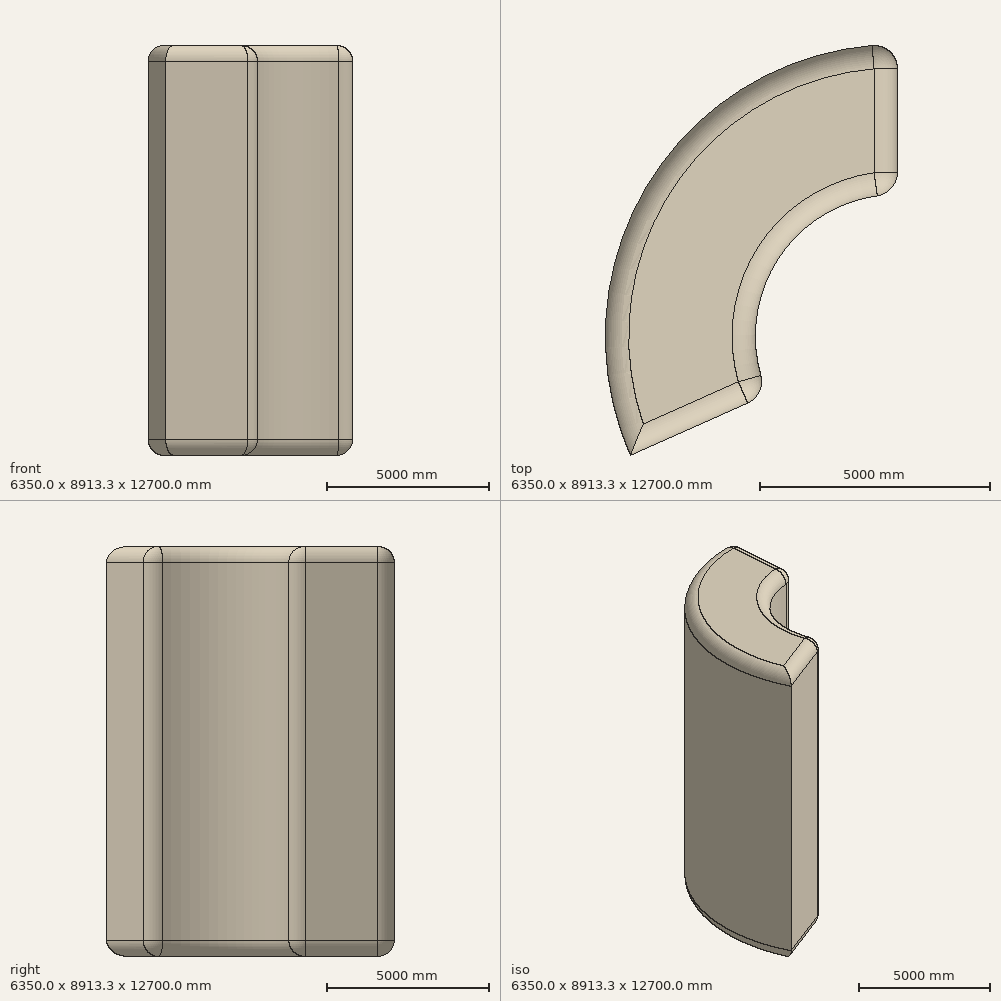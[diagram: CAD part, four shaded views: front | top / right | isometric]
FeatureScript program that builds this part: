
annotation { "Feature Type Name" : "Feature", "Feature Type Description" : "" }
export const myFeature = defineFeature(function(context is Context, id is Id, definition is map)
    precondition{}
    {
        {
            var Q0;
            Q0=qCreatedBy(makeId("Top.planeOp"),FACE);
            var sketch = newSketch(context, id + "F0", { "sketchPlane" : qUnion([Q0])});
            skArc(sketch, "E0", {"start": v(0, 6350) * mm, "mid": v(-5326.35, 3457.24) * mm, "end": v(-5799.83, -2585.43) * mm});
            skLineSegment(sketch, "E1", {"start": v(0, 3087.9) * mm, "end": v(0, 6350) * mm});
            skLineSegment(sketch, "E2", {"start": v(-2820.36, -1257.25) * mm, "end": v(-5799.83, -2585.43) * mm});
            skArc(sketch, "E3", {"start": v(0, 3087.9) * mm, "mid": v(-2590.11, 1681.2) * mm, "end": v(-2820.36, -1257.25) * mm});
            skLineSegment(sketch, "E4", {"start": v(0, 0) * mm, "end": v(10238.72, 163.48) * mm});
            skSolve(sketch);
        }
        {
            var Q0;
            Q0 = qSketchRegion(id + "F0", true);
            extrude(context, id + "F1", {"entities" : qUnion([Q0]), "endBound" : BoundingType.SYMMETRIC, "depth" : 12700 * mm, "offsetDistance" : 25.4 * mm});
        }
        {
            var Q0;
            Q0=makeQuery(id+"F1.opExtrude","CAP_EDGE",EDGE,{"disambiguationData":[OSD([sQuery(id+"F0.wireOp",EDGE,"E0")])],"isStart":false});
            var Q1;
            Q1=makeQuery(id+"F1.opExtrude","CAP_EDGE",EDGE,{"disambiguationData":[OSD([sQuery(id+"F0.wireOp",EDGE,"E3")])],"isStart":false});
            var Q2;
            Q2=makeQuery(id+"F1.opExtrude","SWEPT_EDGE",EDGE,{"disambiguationData":[OSD([sQuery(id+"F0.wireOp",EDGE,"E1"),sQuery(id+"F0.wireOp",EDGE,"E3")])]});
            var Q3;
            Q3=makeQuery(id+"F1.opExtrude","SWEPT_EDGE",EDGE,{"disambiguationData":[OSD([sQuery(id+"F0.wireOp",EDGE,"E0"),sQuery(id+"F0.wireOp",EDGE,"E1")])]});
            var Q4;
            Q4=makeQuery(id+"F1.opExtrude","CAP_EDGE",EDGE,{"disambiguationData":[OSD([sQuery(id+"F0.wireOp",EDGE,"E1")])],"isStart":false});
            var Q5;
            Q5=makeQuery(id+"F1.opExtrude","CAP_EDGE",EDGE,{"disambiguationData":[OSD([sQuery(id+"F0.wireOp",EDGE,"E1")])],"isStart":true});
            var Q6;
            Q6=makeQuery(id+"F1.opExtrude","SWEPT_EDGE",EDGE,{"disambiguationData":[OSD([sQuery(id+"F0.wireOp",EDGE,"E2"),sQuery(id+"F0.wireOp",EDGE,"E3")])]});
            var Q7;
            Q7=makeQuery(id+"F1.opExtrude","CAP_EDGE",EDGE,{"disambiguationData":[OSD([sQuery(id+"F0.wireOp",EDGE,"E2")])],"isStart":false});
            var Q8;
            Q8=makeQuery(id+"F1.opExtrude","CAP_EDGE",EDGE,{"disambiguationData":[OSD([sQuery(id+"F0.wireOp",EDGE,"E3")])],"isStart":true});
            var Q9;
            Q9=makeQuery(id+"F1.opExtrude","CAP_EDGE",EDGE,{"disambiguationData":[OSD([sQuery(id+"F0.wireOp",EDGE,"E0")])],"isStart":true});
            var Q10;
            Q10=makeQuery(id+"F1.opExtrude","CAP_EDGE",EDGE,{"disambiguationData":[OSD([sQuery(id+"F0.wireOp",EDGE,"E2")])],"isStart":true});
            fillet(context, id + "F2", {"entities" : qUnion([Q0, Q1, Q2, Q3, Q4, Q5, Q6, Q7, Q8, Q9, Q10]), "radius" : 508 * mm, "tangentPropagation" : true, "allowEdgeOverflow" : false});
        }
    });
